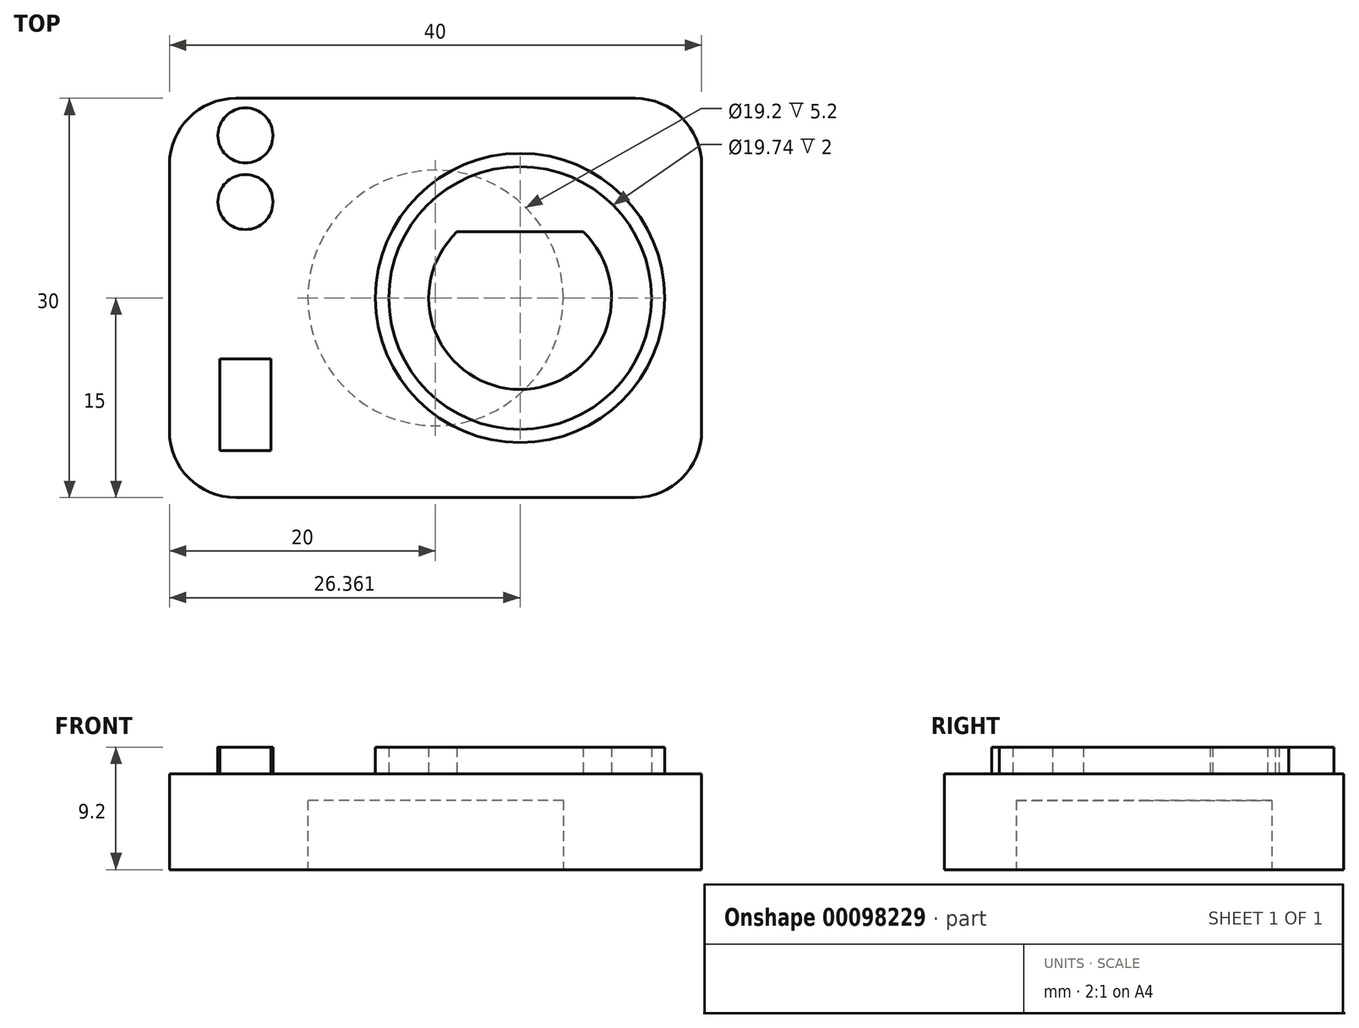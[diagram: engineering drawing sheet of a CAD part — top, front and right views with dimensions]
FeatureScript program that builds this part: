
annotation { "Feature Type Name" : "Feature", "Feature Type Description" : "" }
export const myFeature = defineFeature(function(context is Context, id is Id, definition is map)
    precondition{}
    {
        {
            var Q0;
            Q0=qCreatedBy(makeId("Top.planeOp"),FACE);
            var sketch = newSketch(context, id + "F0", { "sketchPlane" : qUnion([Q0])});
            skCircle(sketch, "E0", {"center": v(0, 0) * mm, "radius": 9.6 * mm});
            skCircle(sketch, "E1.0", {"center": v(0, 0) * mm, "radius": 11.6 * mm});
            skSolve(sketch);
        }
        {
            var Q0;
            Q0=qSketchRegion(id+"F0",true);
            extrude(context, id + "F1", {"entities" : qUnion([Q0]), "depth" : 5.2 * mm});
        }
        {
            var Q0;
            Q0=makeQuery(id+"F1.opExtrude","CAP_FACE",FACE,{"disambiguationData":[OSD([sQuery(id+"F0.wireOp",EDGE,"E0"),sQuery(id+"F0.wireOp",EDGE,"E1.0")])],"isStart":false});
            var sketch = newSketch(context, id + "F2", { "sketchPlane" : qUnion([Q0])});
            skSolve(sketch);
        }
        {
            var Q0;
            Q0=makeQuery(id+"F2.imprint","IMPRINT",FACE,{"disambiguationData":[TD([[makeQuery(id+"F2.imprint","IMPRINT",EDGE,{"derivedFrom":makeQuery(id+"F1.opExtrude","CAP_EDGE",EDGE,{"disambiguationData":[OSD([sQuery(id+"F0.wireOp",EDGE,"E0")])],"isStart":false})}),1.0]])]});
            var Q1;
            Q1=makeQuery(id+"F2.imprint","IMPRINT",FACE,{"disambiguationData":[TD([[makeQuery(id+"F2.imprint","IMPRINT",EDGE,{"derivedFrom":makeQuery(id+"F1.opExtrude","CAP_EDGE",EDGE,{"disambiguationData":[OSD([sQuery(id+"F0.wireOp",EDGE,"E0")])],"isStart":false})}),-1.0]])]});
            extrude(context, id + "F3", {"entities" : qUnion([Q0, Q1]), "operationType" : NewBodyOperationType.ADD, "depth" : 2 * mm});
        }
        {
            var Q0;
            Q0=makeQuery(id+"F3.opExtrude","CAP_FACE",FACE,{"disambiguationData":[OSD([sQuery(id+"F0.wireOp",EDGE,"E1.0")])],"isStart":false});
            var sketch = newSketch(context, id + "F4", { "sketchPlane" : qUnion([Q0])});
            skLineSegment(sketch, "E2.bottom", {"start": v(-20, 15) * mm, "end": v(20, 15) * mm});
            skLineSegment(sketch, "E2.top", {"start": v(-20, -15) * mm, "end": v(20, -15) * mm});
            skLineSegment(sketch, "E2.left", {"start": v(-20, 15) * mm, "end": v(-20, -15) * mm});
            skLineSegment(sketch, "E2.right", {"start": v(20, 15) * mm, "end": v(20, -15) * mm});
            skPoint(sketch, "E2.middle", {"position": v(0, 0) * mm});
            skSolve(sketch);
        }
        {
            var Q0;
            Q0=makeQuery(id+"F4.imprint","IMPRINT",FACE,{"disambiguationData":[TD([[makeQuery(id+"F4.imprint","IMPRINT",EDGE,{"derivedFrom":sQuery(id+"F4.wireOp",EDGE,"E2.bottom")}),-1.0]])]});
            extrude(context, id + "F5", {"entities" : qUnion([Q0]), "operationType" : NewBodyOperationType.ADD, "oppositeDirection" : true, "depth" : 7.2 * mm});
        }
        {
            var Q0;
            Q0=makeQuery(id+"F5.opExtrude","SWEPT_EDGE",EDGE,{"disambiguationData":[OSD([sQuery(id+"F4.wireOp",EDGE,"E2.top"),sQuery(id+"F4.wireOp",EDGE,"E2.left")])]});
            var Q1;
            Q1=makeQuery(id+"F5.opExtrude","SWEPT_EDGE",EDGE,{"disambiguationData":[OSD([sQuery(id+"F4.wireOp",EDGE,"E2.bottom"),sQuery(id+"F4.wireOp",EDGE,"E2.left")])]});
            var Q2;
            Q2=makeQuery(id+"F5.opExtrude","SWEPT_EDGE",EDGE,{"disambiguationData":[OSD([sQuery(id+"F4.wireOp",EDGE,"E2.top"),sQuery(id+"F4.wireOp",EDGE,"E2.right")])]});
            var Q3;
            Q3=makeQuery(id+"F5.opExtrude","SWEPT_EDGE",EDGE,{"disambiguationData":[OSD([sQuery(id+"F4.wireOp",EDGE,"E2.bottom"),sQuery(id+"F4.wireOp",EDGE,"E2.right")])]});
            fillet(context, id + "F6", {"entities" : qUnion([Q0, Q1, Q2, Q3]), "radius" : 5 * mm, "tangentPropagation" : true, "allowEdgeOverflow" : false});
        }
        {
            var Q0;
            {var subQ0=sQuery(id+"F0.wireOp",EDGE,"E1.0");Q0=makeQuery(id+"F5.boolean.opBoolean","MERGE",FACE,{"derivedFrom":[makeQuery(id+"F3.opExtrude","CAP_FACE",FACE,{"disambiguationData":[OSD([subQ0])],"isStart":false}),makeQuery(id+"F5.opExtrude","CAP_FACE",FACE,{"disambiguationData":[OSD([subQ0,sQuery(id+"F4.wireOp",EDGE,"E2.bottom"),sQuery(id+"F4.wireOp",EDGE,"E2.top"),sQuery(id+"F4.wireOp",EDGE,"E2.left"),sQuery(id+"F4.wireOp",EDGE,"E2.right")])],"isStart":true})]});}
            var sketch = newSketch(context, id + "F7", { "sketchPlane" : qUnion([Q0])});
            skLineSegment(sketch, "E3", {"start": v(-14.28, -16.7) * mm, "end": v(-14.28, 21.08) * mm, "construction": true});
            skCircle(sketch, "E4", {"center": v(-14.28, 12.21) * mm, "radius": 2.07 * mm});
            skCircle(sketch, "E5", {"center": v(-14.28, 7.21) * mm, "radius": 2.07 * mm});
            skCircle(sketch, "E6", {"center": v(6.36, 0) * mm, "radius": 9.87 * mm});
            skCircle(sketch, "E7.0", {"center": v(6.36, 0) * mm, "radius": 6.87 * mm});
            skLineSegment(sketch, "E8", {"start": v(1.62, 4.97) * mm, "end": v(11.1, 4.97) * mm});
            skCircle(sketch, "E9.0", {"center": v(6.36, 0) * mm, "radius": 10.87 * mm});
            skLineSegment(sketch, "E10.bottom", {"start": v(-16.2, -11.46) * mm, "end": v(-12.36, -11.46) * mm});
            skLineSegment(sketch, "E10.top", {"start": v(-16.2, -4.57) * mm, "end": v(-12.36, -4.57) * mm});
            skLineSegment(sketch, "E10.left", {"start": v(-16.2, -11.46) * mm, "end": v(-16.2, -4.57) * mm});
            skLineSegment(sketch, "E10.right", {"start": v(-12.36, -11.46) * mm, "end": v(-12.36, -4.57) * mm});
            skPoint(sketch, "E10.middle", {"position": v(-14.28, -8.02) * mm});
            skSolve(sketch);
        }
        {
            var Q0;
            {var subQ0=sQuery(id+"F7.wireOp",EDGE,"E8");Q0=makeQuery(id+"F7.imprint","IMPRINT",FACE,{"disambiguationData":[TD([[makeQuery(id+"F7.imprint","IMPRINT",EDGE,{"derivedFrom":subQ0}),-1.0]])]});}
            var Q1;
            Q1=makeQuery(id+"F7.imprint","IMPRINT",FACE,{"disambiguationData":[TD([[makeQuery(id+"F7.imprint","IMPRINT",EDGE,{"derivedFrom":sQuery(id+"F7.wireOp",EDGE,"E6")}),-1.0]])]});
            var Q2;
            Q2=makeQuery(id+"F7.imprint","IMPRINT",FACE,{"disambiguationData":[TD([[makeQuery(id+"F7.imprint","IMPRINT",EDGE,{"derivedFrom":sQuery(id+"F7.wireOp",EDGE,"E10.bottom")}),1.0]])]});
            var Q3;
            Q3=makeQuery(id+"F7.imprint","IMPRINT",FACE,{"disambiguationData":[TD([[makeQuery(id+"F7.imprint","IMPRINT",EDGE,{"derivedFrom":sQuery(id+"F7.wireOp",EDGE,"E5")}),1.0]])]});
            var Q4;
            Q4=makeQuery(id+"F7.imprint","IMPRINT",FACE,{"disambiguationData":[TD([[makeQuery(id+"F7.imprint","IMPRINT",EDGE,{"derivedFrom":sQuery(id+"F7.wireOp",EDGE,"E4")}),1.0]])]});
            extrude(context, id + "F8", {"entities" : qUnion([Q0, Q1, Q2, Q3, Q4]), "operationType" : NewBodyOperationType.ADD, "depth" : 2 * mm});
        }
    });
